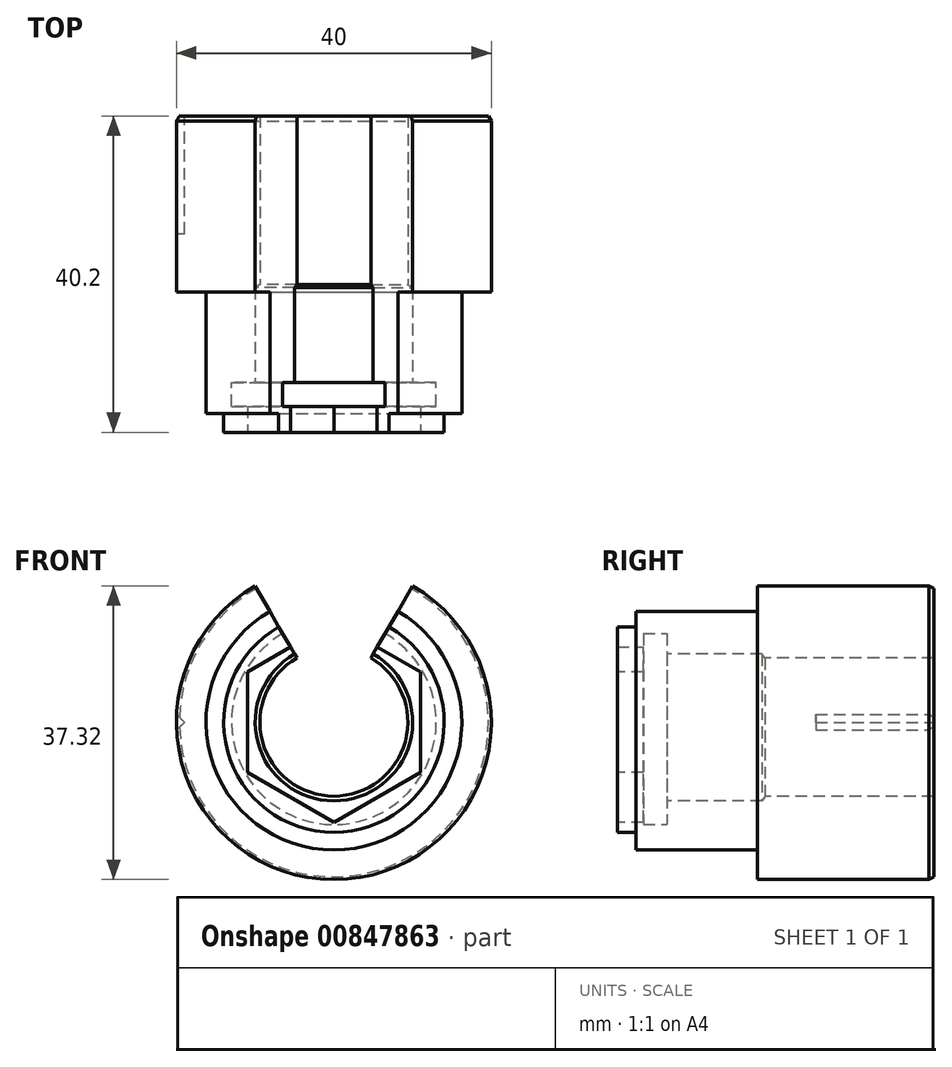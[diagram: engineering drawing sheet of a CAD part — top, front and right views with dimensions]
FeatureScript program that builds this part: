
annotation { "Feature Type Name" : "Feature", "Feature Type Description" : "" }
export const myFeature = defineFeature(function(context is Context, id is Id, definition is map)
    precondition{}
    {
        {
            var Q0;
            Q0=qCreatedBy(makeId("Front.planeOp"),FACE);
            var sketch = newSketch(context, id + "F0", { "sketchPlane" : qUnion([Q0])});
            skCircle(sketch, "E0", {"center": v(0, 0) * mm, "radius": 20 * mm});
            skSolve(sketch);
        }
        {
            var Q0;
            Q0=makeQuery(id+"F0.imprint","IMPRINT",FACE,{"disambiguationData":[TD([[makeQuery(id+"F0.imprint","IMPRINT",EDGE,{"derivedFrom":sQuery(id+"F0.wireOp",EDGE,"E0")}),1.0]])]});
            extrude(context, id + "F1", {"entities" : qUnion([Q0]), "depth" : 40.2 * mm, "offsetDistance" : 25 * mm});
        }
        {
            var Q0;
            Q0=makeQuery(id+"F1.opExtrude","CAP_FACE",FACE,{"disambiguationData":[OSD([sQuery(id+"F0.wireOp",EDGE,"E0")])],"isStart":false});
            var sketch = newSketch(context, id + "F2", { "sketchPlane" : qUnion([Q0])});
            skCircle(sketch, "E1", {"center": v(0, 0) * mm, "radius": 16.25 * mm});
            skCircle(sketch, "E2.0", {"center": v(0, 0) * mm, "radius": 20 * mm});
            skSolve(sketch);
        }
        {
            var Q0;
            Q0 = qSketchRegion(id + "F2", true);
            extrude(context, id + "F3", {"entities" : qUnion([Q0]), "operationType" : NewBodyOperationType.REMOVE, "oppositeDirection" : true, "depth" : 17.8 * mm, "offsetDistance" : 25 * mm});
        }
        {
            var Q0;
            Q0=makeQuery(id+"F1.opExtrude","CAP_FACE",FACE,{"disambiguationData":[OSD([sQuery(id+"F0.wireOp",EDGE,"E0")])],"isStart":false});
            var sketch = newSketch(context, id + "F4", { "sketchPlane" : qUnion([Q0])});
            skArc(sketch, "E3", {"start": v(-4.7, 8.14) * mm, "mid": v(0, -9.4) * mm, "end": v(4.7, 8.14) * mm});
            skLineSegment(sketch, "E4", {"start": v(4.7, 8.14) * mm, "end": v(10, 17.32) * mm});
            skLineSegment(sketch, "E5", {"start": v(-4.7, 8.14) * mm, "end": v(-10, 17.32) * mm});
            skArc(sketch, "E6.0", {"start": v(10, 17.32) * mm, "mid": v(0, 20) * mm, "end": v(-10, 17.32) * mm});
            skSolve(sketch);
        }
        {
            var Q0;
            Q0 = qSketchRegion(id + "F4", true);
            extrude(context, id + "F5", {"entities" : qUnion([Q0]), "operationType" : NewBodyOperationType.REMOVE, "endBound" : BoundingType.THROUGH_ALL, "oppositeDirection" : true, "depth" : 25 * mm, "offsetDistance" : 25 * mm});
        }
        {
            var Q0;
            Q0=makeQuery(id+"F1.opExtrude","CAP_FACE",FACE,{"disambiguationData":[OSD([sQuery(id+"F0.wireOp",EDGE,"E0")])],"isStart":false});
            cPlane(context, id + "F6", {"entities" : qUnion([Q0]), "cplaneType" : CPlaneType.OFFSET, "offset" : 6.3 * mm, "oppositeDirection" : true, "width" : 150 * mm, "height" : 150 * mm});
        }
        {
            var Q0;
            Q0=qCreatedBy(id+"F6.planeOp",FACE);
            var sketch = newSketch(context, id + "F7", { "sketchPlane" : qUnion([Q0])});
            skCircle(sketch, "E7", {"center": v(0, 0) * mm, "radius": 13 * mm});
            skSolve(sketch);
        }
        {
            var Q0;
            Q0 = qSketchRegion(id + "F7", true);
            extrude(context, id + "F8", {"entities" : qUnion([Q0]), "operationType" : NewBodyOperationType.REMOVE, "depth" : 3 * mm, "offsetDistance" : 25 * mm});
        }
        {
            var Q0;
            Q0=makeQuery(id+"F1.opExtrude","CAP_FACE",FACE,{"disambiguationData":[OSD([sQuery(id+"F0.wireOp",EDGE,"E0")])],"isStart":false});
            var sketch = newSketch(context, id + "F9", { "sketchPlane" : qUnion([Q0])});
            skCircle(sketch, "E8.cCircle", {"center": v(0, 0) * mm, "radius": 11 * mm, "construction": true});
            skLineSegment(sketch, "E8.0", {"start": v(11, 6.35) * mm, "end": v(11, -6.35) * mm});
            skLineSegment(sketch, "E8.1", {"start": v(11, -6.35) * mm, "end": v(0, -12.7) * mm});
            skLineSegment(sketch, "E8.2", {"start": v(0, -12.7) * mm, "end": v(-11, -6.35) * mm});
            skLineSegment(sketch, "E8.3", {"start": v(-11, -6.35) * mm, "end": v(-11, 6.35) * mm});
            skLineSegment(sketch, "E8.4", {"start": v(-11, 6.35) * mm, "end": v(0, 12.7) * mm});
            skLineSegment(sketch, "E8.5", {"start": v(0, 12.7) * mm, "end": v(11, 6.35) * mm});
            skPoint(sketch, "E8.0.midPoint", {"position": v(11, 0) * mm});
            skSolve(sketch);
        }
        {
            var Q0;
            Q0 = qSketchRegion(id + "F9", true);
            extrude(context, id + "F10", {"entities" : qUnion([Q0]), "operationType" : NewBodyOperationType.REMOVE, "oppositeDirection" : true, "depth" : 5 * mm, "offsetDistance" : 25 * mm});
        }
        {
            var Q0;
            Q0=makeQuery(id+"F1.opExtrude","CAP_FACE",FACE,{"disambiguationData":[OSD([sQuery(id+"F0.wireOp",EDGE,"E0")])],"isStart":false});
            var sketch = newSketch(context, id + "F11", { "sketchPlane" : qUnion([Q0])});
            skCircle(sketch, "E9", {"center": v(0, 0) * mm, "radius": 14 * mm});
            skCircle(sketch, "E10", {"center": v(0, 0) * mm, "radius": 16.25 * mm});
            skSolve(sketch);
        }
        {
            var Q0;
            Q0 = qSketchRegion(id + "F11", true);
            extrude(context, id + "F12", {"entities" : qUnion([Q0]), "operationType" : NewBodyOperationType.REMOVE, "oppositeDirection" : true, "depth" : 2.4 * mm, "offsetDistance" : 25 * mm});
        }
        {
            var Q0;
            Q0=makeQuery(id+"F1.opExtrude","CAP_FACE",FACE,{"disambiguationData":[OSD([sQuery(id+"F0.wireOp",EDGE,"E0")])],"isStart":true});
            var sketch = newSketch(context, id + "F13", { "sketchPlane" : qUnion([Q0])});
            skPoint(sketch, "E11.orphan", {"position": v(10, 17.32) * mm});
            skLineSegment(sketch, "E12.MirrorCS", {"start": v(19, 0) * mm, "end": v(19.98, -0.98) * mm});
            skLineSegment(sketch, "E13.MirrorCS", {"start": v(19, 0) * mm, "end": v(19.98, 0.98) * mm});
            skArc(sketch, "E14.MirrorCS", {"start": v(19.98, -0.98) * mm, "mid": v(20, 0) * mm, "end": v(19.98, 0.98) * mm});
            skSolve(sketch);
        }
        {
            var Q0;
            Q0 = qSketchRegion(id + "F13", true);
            extrude(context, id + "F14", {"entities" : qUnion([Q0]), "operationType" : NewBodyOperationType.REMOVE, "oppositeDirection" : true, "depth" : 15 * mm, "offsetDistance" : 25 * mm});
        }
        {
            var Q0;
            Q0=qCreatedBy(makeId("Right.planeOp"),FACE);
            var sketch = newSketch(context, id + "F15", { "sketchPlane" : qUnion([Q0])});
            skLineSegment(sketch, "E15", {"start": v(0, -20) * mm, "end": v(-0.64, -20) * mm});
            skLineSegment(sketch, "E16", {"start": v(0, -19.63) * mm, "end": v(-0.64, -20) * mm});
            skLineSegment(sketch, "E17.0", {"start": v(0, -20) * mm, "end": v(0, -19.63) * mm});
            skPoint(sketch, "E18.orphan", {"position": v(0, 17.32) * mm});
            skSolve(sketch);
        }
        {
            var Q0;
            Q0 = qSketchRegion(id + "F15", true);
            var Q1;
            Q1=makeQuery(id+"F12.boolean.opBoolean","COPY",FACE,{"derivedFrom":makeQuery(id+"F12.opExtrude","SWEPT_FACE",FACE,{"disambiguationData":[OSD([sQuery(id+"F11.wireOp",EDGE,"E9")])]})});
            revolve(context, id + "F16", {"operationType" : NewBodyOperationType.REMOVE, "surfaceOperationType" : NewSurfaceOperationType.NEW, "entities" : qUnion([Q0]), "axis" : qUnion([Q1]), "revolveType" : RevolveType.FULL, "oppositeDirection" : true});
        }
        {
            var Q0;
            Q0=makeQuery(id+"F1.opExtrude","CAP_FACE",FACE,{"disambiguationData":[OSD([sQuery(id+"F0.wireOp",EDGE,"E0")])],"isStart":false});
            cPlane(context, id + "F17", {"entities" : qUnion([Q0]), "cplaneType" : CPlaneType.OFFSET, "offset" : 18.4 * mm, "oppositeDirection" : true, "width" : 150 * mm, "height" : 150 * mm});
        }
        {
            var Q0;
            Q0=makeQuery(id+"F1.opExtrude","CAP_FACE",FACE,{"disambiguationData":[OSD([sQuery(id+"F0.wireOp",EDGE,"E0")])],"isStart":false});
            var sketch = newSketch(context, id + "F18", { "sketchPlane" : qUnion([Q0])});
            skCircle(sketch, "E19", {"center": v(0, 0) * mm, "radius": 10 * mm});
            skSolve(sketch);
        }
        {
            var Q0;
            Q0 = qSketchRegion(id + "F18", true);
            extrude(context, id + "F19", {"entities" : qUnion([Q0]), "operationType" : NewBodyOperationType.REMOVE, "oppositeDirection" : true, "depth" : 18.4 * mm, "offsetDistance" : 25 * mm});
        }
        {
            var Q0;
            Q0=qCreatedBy(makeId("Top.planeOp"),FACE);
            var sketch = newSketch(context, id + "F20", { "sketchPlane" : qUnion([Q0])});
            skPoint(sketch, "E20.orphan", {"position": v(-20, -22.4) * mm});
            skPoint(sketch, "E21.0.start.orphan", {"position": v(-9.4, -21.8) * mm});
            skLineSegment(sketch, "E22.trimOffspring", {"start": v(-9.4, -21.8) * mm, "end": v(-10, -21.8) * mm});
            skLineSegment(sketch, "E23", {"start": v(-10, -21.8) * mm, "end": v(-9.4, -21.45) * mm});
            skLineSegment(sketch, "E24", {"start": v(-9.4, -21.8) * mm, "end": v(-9.4, -21.45) * mm});
            skSolve(sketch);
        }
        {
            var Q0;
            Q0 = qSketchRegion(id + "F20", true);
            var Q1;
            Q1=makeQuery(id+"F19.boolean.opBoolean","COPY",FACE,{"derivedFrom":makeQuery(id+"F19.opExtrude","SWEPT_FACE",FACE,{"disambiguationData":[OSD([sQuery(id+"F18.wireOp",EDGE,"E19")])]})});
            revolve(context, id + "F21", {"operationType" : NewBodyOperationType.REMOVE, "surfaceOperationType" : NewSurfaceOperationType.NEW, "entities" : qUnion([Q0]), "axis" : qUnion([Q1]), "revolveType" : RevolveType.FULL, "oppositeDirection" : true});
        }
    });
